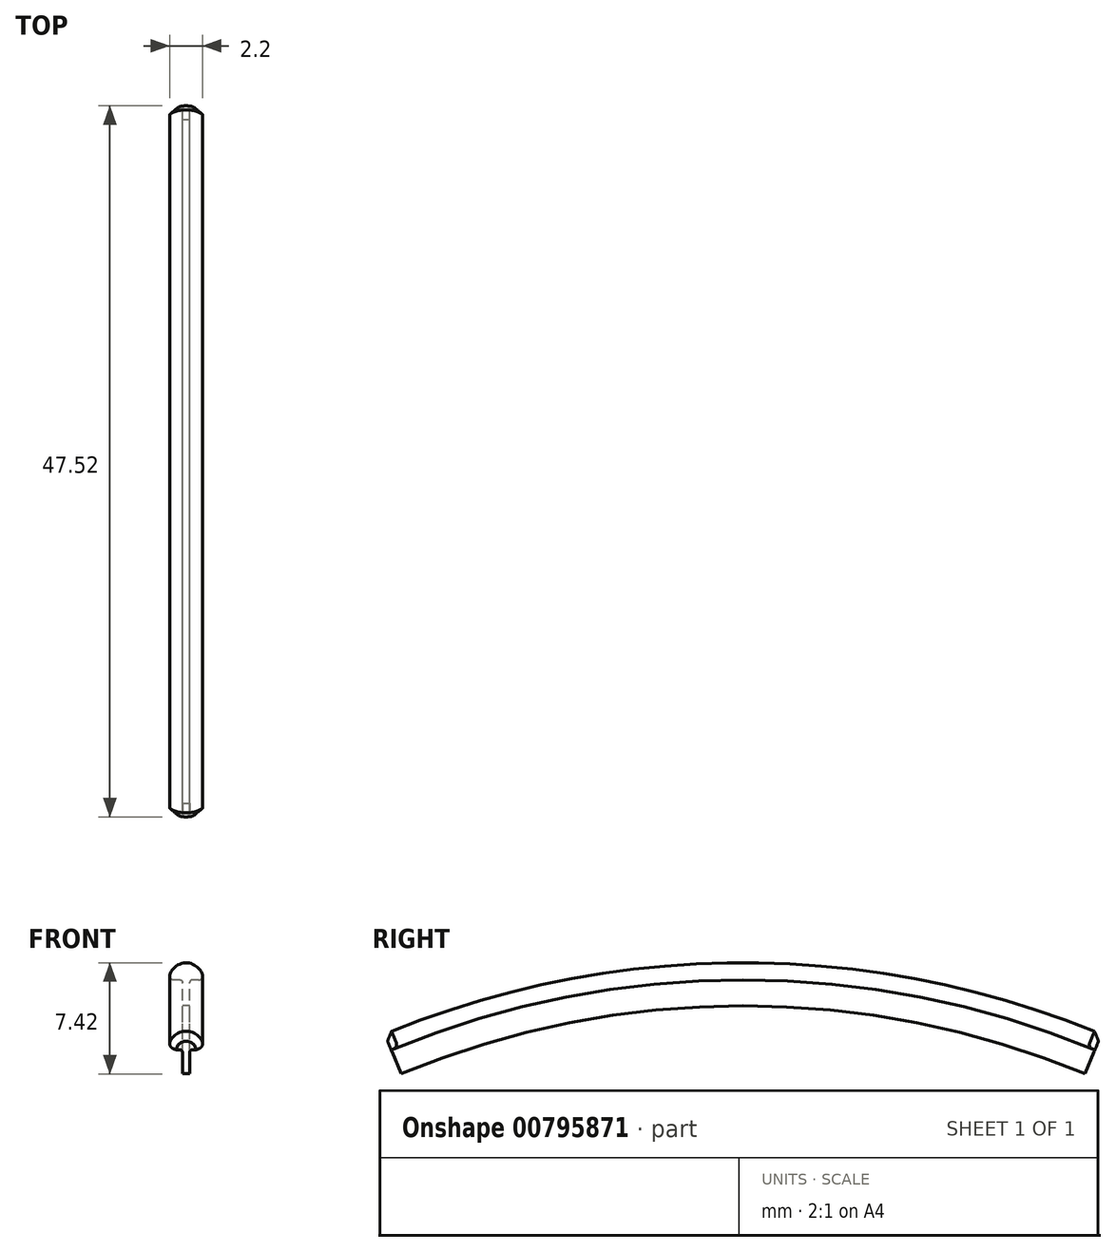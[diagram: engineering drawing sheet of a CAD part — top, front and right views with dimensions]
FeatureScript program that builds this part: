
annotation { "Feature Type Name" : "Feature", "Feature Type Description" : "" }
export const myFeature = defineFeature(function(context is Context, id is Id, definition is map)
    precondition{}
    {
        {
            var Q0;
            Q0=qCreatedBy(makeId("Front.planeOp"),FACE);
            var sketch = newSketch(context, id + "F0", { "sketchPlane" : qUnion([Q0])});
            skLineSegment(sketch, "E0", {"start": v(-0.25, 0) * mm, "end": v(0.25, 0) * mm});
            skLineSegment(sketch, "E1", {"start": v(0.25, 0) * mm, "end": v(0.25, 1.58) * mm});
            skLineSegment(sketch, "E2", {"start": v(-0.25, 0) * mm, "end": v(-0.25, 1.58) * mm});
            skArc(sketch, "E3", {"start": v(-1.1, 2.05) * mm, "mid": v(0, 2.87) * mm, "end": v(1.1, 2.05) * mm});
            skLineSegment(sketch, "E4", {"start": v(-0.55, 2.87) * mm, "end": v(0.52, 2.87) * mm, "construction": true});
            skLineSegment(sketch, "E5", {"start": v(-0.85, 1.73) * mm, "end": v(-0.4, 1.73) * mm});
            skLineSegment(sketch, "E6", {"start": v(0.85, 1.73) * mm, "end": v(0.4, 1.73) * mm});
            skPoint(sketch, "E7.visualSharp", {"position": v(1.14, 1.73) * mm});
            skArc(sketch, "E7.filletArc", {"start": v(0.85, 1.73) * mm, "mid": v(1.05, 1.83) * mm, "end": v(1.1, 2.05) * mm});
            skPoint(sketch, "E8.visualSharp", {"position": v(-1.14, 1.73) * mm});
            skArc(sketch, "E8.filletArc", {"start": v(-1.1, 2.05) * mm, "mid": v(-1.05, 1.83) * mm, "end": v(-0.85, 1.73) * mm});
            skPoint(sketch, "E9.visualSharp", {"position": v(0.25, 1.73) * mm});
            skArc(sketch, "E9.filletArc", {"start": v(0.4, 1.73) * mm, "mid": v(0.3, 1.69) * mm, "end": v(0.25, 1.58) * mm});
            skPoint(sketch, "E10.visualSharp", {"position": v(-0.25, 1.73) * mm});
            skArc(sketch, "E10.filletArc", {"start": v(-0.25, 1.58) * mm, "mid": v(-0.3, 1.69) * mm, "end": v(-0.4, 1.73) * mm});
            skLineSegment(sketch, "E11", {"start": v(-2.62, -59.7) * mm, "end": v(2.54, -59.7) * mm, "construction": true});
            skSolve(sketch);
        }
        {
            var Q0;
            Q0 = qSketchRegion(id + "F0", true);
            var Q1;
            Q1=sQuery(id+"F0.wireOp",EDGE,"E11");
            revolve(context, id + "F1", {"surfaceOperationType" : NewSurfaceOperationType.NEW, "entities" : qUnion([Q0]), "axis" : qUnion([Q1]), "revolveType" : RevolveType.SYMMETRIC, "angle" : 45 * degree});
        }
        {
            var Q0;
            Q0=makeQuery(id+"F1.opRevolve","CAP_EDGE",EDGE,{"disambiguationData":[OSD([sQuery(id+"F0.wireOp",EDGE,"E3")])],"isStart":false});
            chamfer(context, id + "F2", {"entities" : qUnion([Q0]), "width" : 0.5 * mm});
        }
        {
            var Q0;
            Q0=makeQuery(id+"F1.opRevolve","CAP_EDGE",EDGE,{"disambiguationData":[OSD([sQuery(id+"F0.wireOp",EDGE,"E3")])],"isStart":true});
            chamfer(context, id + "F3", {"entities" : qUnion([Q0]), "width" : 0.5 * mm});
        }
    });
